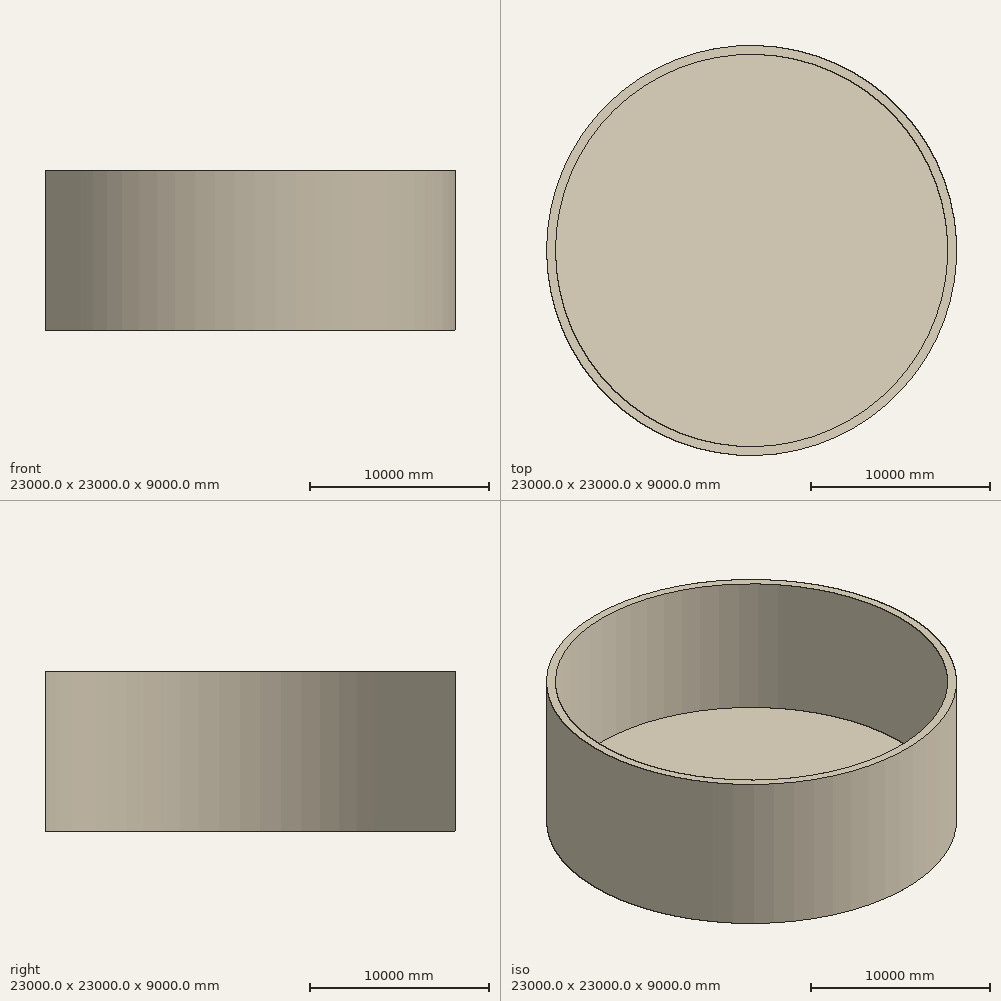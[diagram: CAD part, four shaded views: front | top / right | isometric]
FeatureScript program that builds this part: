
annotation { "Feature Type Name" : "Feature", "Feature Type Description" : "" }
export const myFeature = defineFeature(function(context is Context, id is Id, definition is map)
    precondition{}
    {
        {
            var Q0;
            Q0=qCreatedBy(makeId("Front.planeOp"),FACE);
            var sketch = newSketch(context, id + "F0", { "sketchPlane" : qUnion([Q0])});
            skLineSegment(sketch, "E0", {"start": v(0, 0) * mm, "end": v(-11000, 0) * mm});
            skLineSegment(sketch, "E1", {"start": v(-11000, 0) * mm, "end": v(-11000, 8000) * mm});
            skLineSegment(sketch, "E2", {"start": v(-11000, 8000) * mm, "end": v(-11500, 8000) * mm});
            skLineSegment(sketch, "E3", {"start": v(-11500, 8000) * mm, "end": v(-11500, -1000) * mm});
            skLineSegment(sketch, "E4", {"start": v(-11500, -1000) * mm, "end": v(0, -1000) * mm});
            skLineSegment(sketch, "E5", {"start": v(0, -1000) * mm, "end": v(0, 0) * mm});
            skSolve(sketch);
        }
        {
            var Q0;
            Q0=makeQuery(id+"F0.imprint","IMPRINT",FACE,{"disambiguationData":[TD([[makeQuery(id+"F0.imprint","IMPRINT",EDGE,{"derivedFrom":sQuery(id+"F0.wireOp",EDGE,"E0")}),1.0]])]});
            var Q1;
            Q1=sQuery(id+"F0.wireOp",EDGE,"E5");
            revolve(context, id + "F1", {"entities" : qUnion([Q0]), "axis" : qUnion([Q1]), "revolveType" : RevolveType.FULL});
        }
    });
